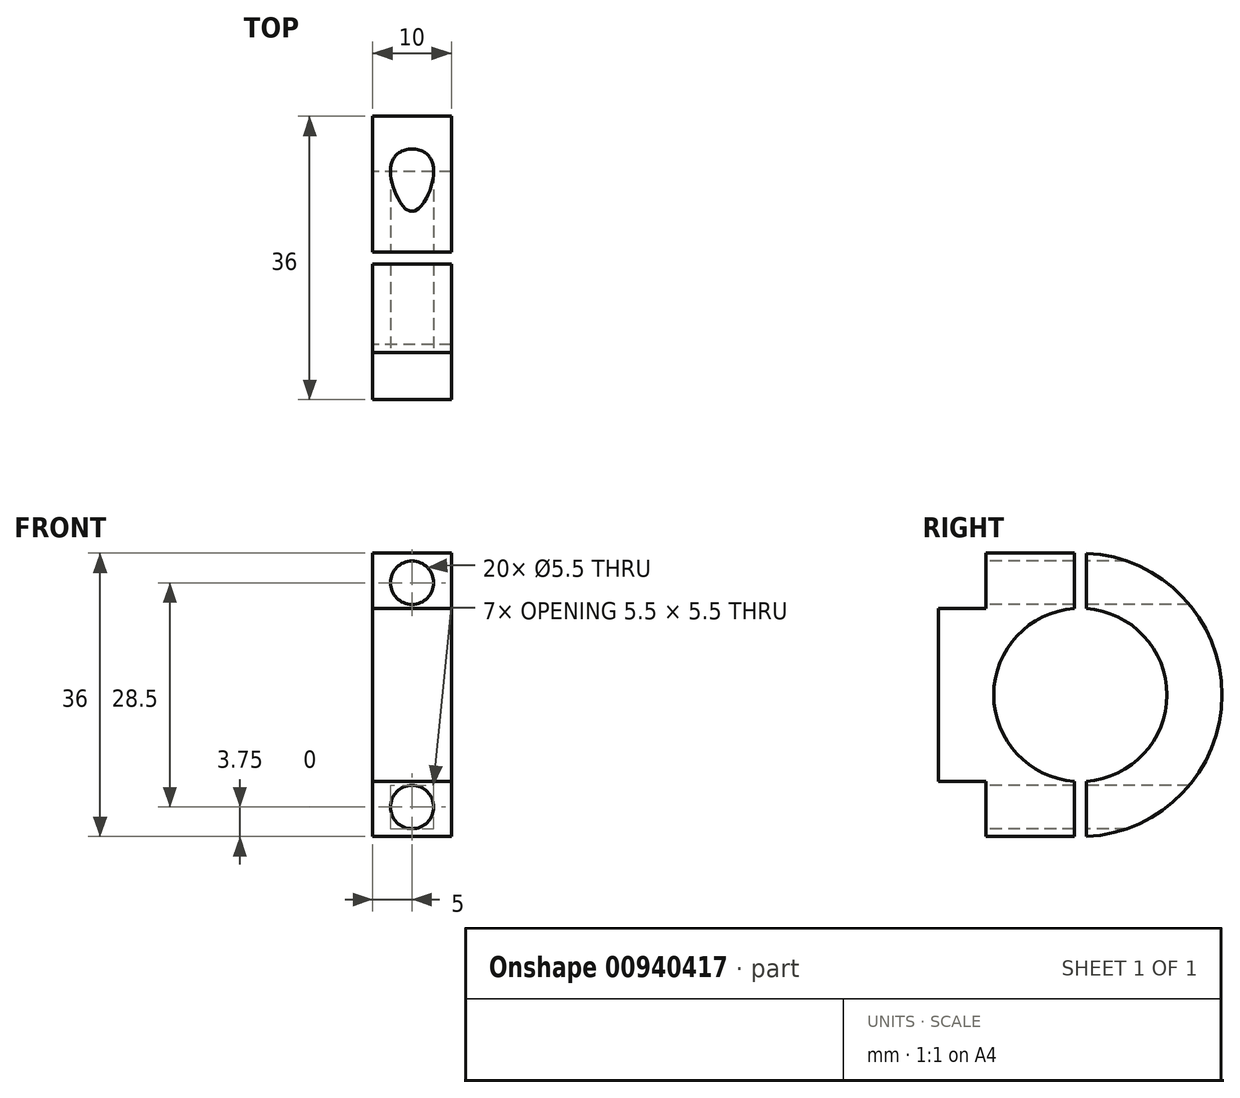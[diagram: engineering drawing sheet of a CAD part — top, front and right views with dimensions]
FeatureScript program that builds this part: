
annotation { "Feature Type Name" : "Feature", "Feature Type Description" : "" }
export const myFeature = defineFeature(function(context is Context, id is Id, definition is map)
    precondition{}
    {
        {
            var Q0;
            Q0=qCreatedBy(makeId("Right.planeOp"),FACE);
            var sketch = newSketch(context, id + "F0", { "sketchPlane" : qUnion([Q0])});
            skArc(sketch, "E0", {"start": v(-0.75, 10.97) * mm, "mid": v(-11, 0) * mm, "end": v(-0.75, -10.97) * mm});
            skArc(sketch, "E1", {"start": v(0.75, -17.98) * mm, "mid": v(18, 0) * mm, "end": v(0.75, 17.98) * mm});
            skLineSegment(sketch, "E2", {"start": v(-0.75, 18) * mm, "end": v(-12, 18) * mm});
            skLineSegment(sketch, "E3", {"start": v(-18, 10.97) * mm, "end": v(-18, -10.97) * mm});
            skLineSegment(sketch, "E4", {"start": v(-12, -18) * mm, "end": v(-0.75, -18) * mm});
            skLineSegment(sketch, "E5", {"start": v(-0.75, 18) * mm, "end": v(-0.75, 10.97) * mm});
            skLineSegment(sketch, "E6", {"start": v(0.75, 17.98) * mm, "end": v(0.75, 10.97) * mm});
            skLineSegment(sketch, "E7.trimOffspring", {"start": v(-0.75, -10.97) * mm, "end": v(-0.75, -18) * mm});
            skLineSegment(sketch, "E8.trimOffspring", {"start": v(0.75, -10.97) * mm, "end": v(0.75, -17.98) * mm});
            skArc(sketch, "E9.trimOffspring", {"start": v(0.75, -10.97) * mm, "mid": v(11, 0) * mm, "end": v(0.75, 10.97) * mm});
            skPoint(sketch, "E10.orphan", {"position": v(0, 18) * mm});
            skLineSegment(sketch, "E11.top", {"start": v(-18, 10.97) * mm, "end": v(-12, 10.97) * mm});
            skLineSegment(sketch, "E11.right", {"start": v(-12, 18) * mm, "end": v(-12, 10.97) * mm});
            skLineSegment(sketch, "E12.top", {"start": v(-18, -10.97) * mm, "end": v(-12, -10.97) * mm});
            skLineSegment(sketch, "E12.right", {"start": v(-12, -18) * mm, "end": v(-12, -10.97) * mm});
            skSolve(sketch);
        }
        {
            var Q0;
            Q0 = qSketchRegion(id + "F0", true);
            extrude(context, id + "F1", {"entities" : qUnion([Q0]), "endBound" : BoundingType.SYMMETRIC, "depth" : 10 * mm, "offsetDistance" : 25 * mm});
        }
        {
            var Q0;
            Q0=qCreatedBy(makeId("Front.planeOp"),FACE);
            var sketch = newSketch(context, id + "F2", { "sketchPlane" : qUnion([Q0])});
            skCircle(sketch, "E13", {"center": v(0, 14.25) * mm, "radius": 2.75 * mm});
            skCircle(sketch, "E14", {"center": v(0, -14.25) * mm, "radius": 2.75 * mm});
            skSolve(sketch);
        }
        {
            var Q0;
            Q0 = qSketchRegion(id + "F2", true);
            extrude(context, id + "F3", {"entities" : qUnion([Q0]), "operationType" : NewBodyOperationType.REMOVE, "endBound" : BoundingType.SYMMETRIC, "oppositeDirection" : true, "depth" : 50 * mm, "offsetDistance" : 25 * mm});
        }
    });
